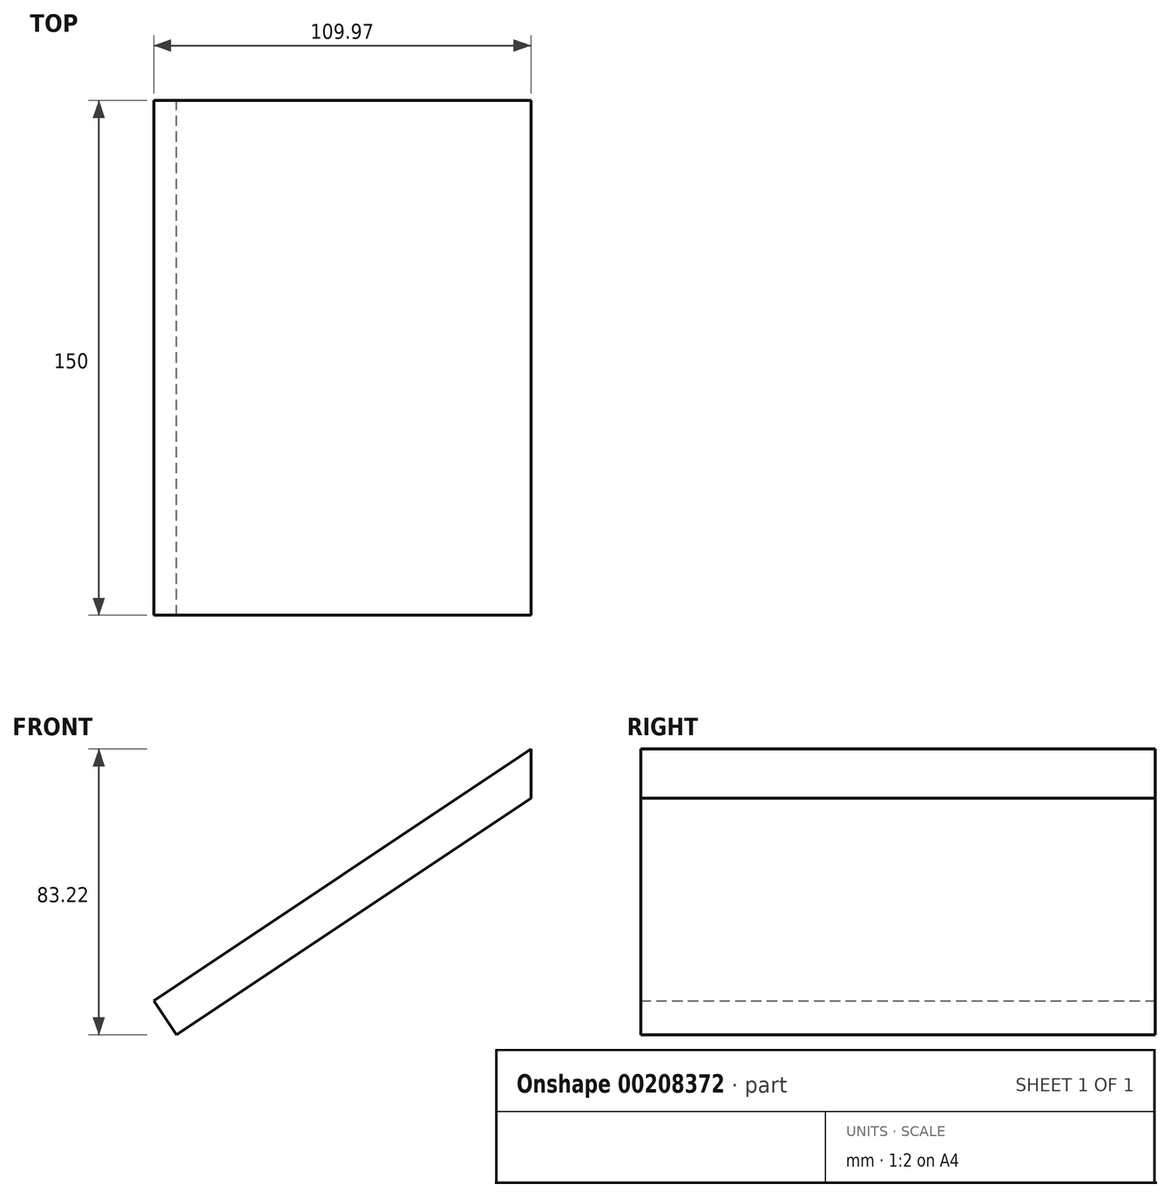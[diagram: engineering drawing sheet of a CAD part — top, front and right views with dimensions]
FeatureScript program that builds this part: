
annotation { "Feature Type Name" : "Feature", "Feature Type Description" : "" }
export const myFeature = defineFeature(function(context is Context, id is Id, definition is map)
    precondition{}
    {
        {
            var Q0;
            Q0=qCreatedBy(makeId("Front.planeOp"),FACE);
            var sketch = newSketch(context, id + "F0", { "sketchPlane" : qUnion([Q0])});
            skLineSegment(sketch, "E0", {"start": v(-75, 100) * mm, "end": v(0, 150) * mm});
            skLineSegment(sketch, "E1", {"start": v(-75, 100) * mm, "end": v(-103.36, 81.1) * mm});
            skLineSegment(sketch, "E2", {"start": v(-103.36, 81.1) * mm, "end": v(-109.97, 91) * mm});
            skLineSegment(sketch, "E3", {"start": v(-109.97, 91) * mm, "end": v(0, 164.31) * mm});
            skLineSegment(sketch, "E4", {"start": v(0, 164.31) * mm, "end": v(0, 150) * mm});
            skPoint(sketch, "E5.bottom.start.orphan", {"position": v(-75, 0) * mm});
            skSolve(sketch);
        }
        {
            var Q0;
            Q0=makeQuery(id+"F0.imprint","IMPRINT",FACE,{"disambiguationData":[TD([[makeQuery(id+"F0.imprint","IMPRINT",EDGE,{"derivedFrom":sQuery(id+"F0.wireOp",EDGE,"E0")}),1.0]])]});
            extrude(context, id + "F1", {"entities" : qUnion([Q0]), "depth" : 150 * mm});
        }
    });
